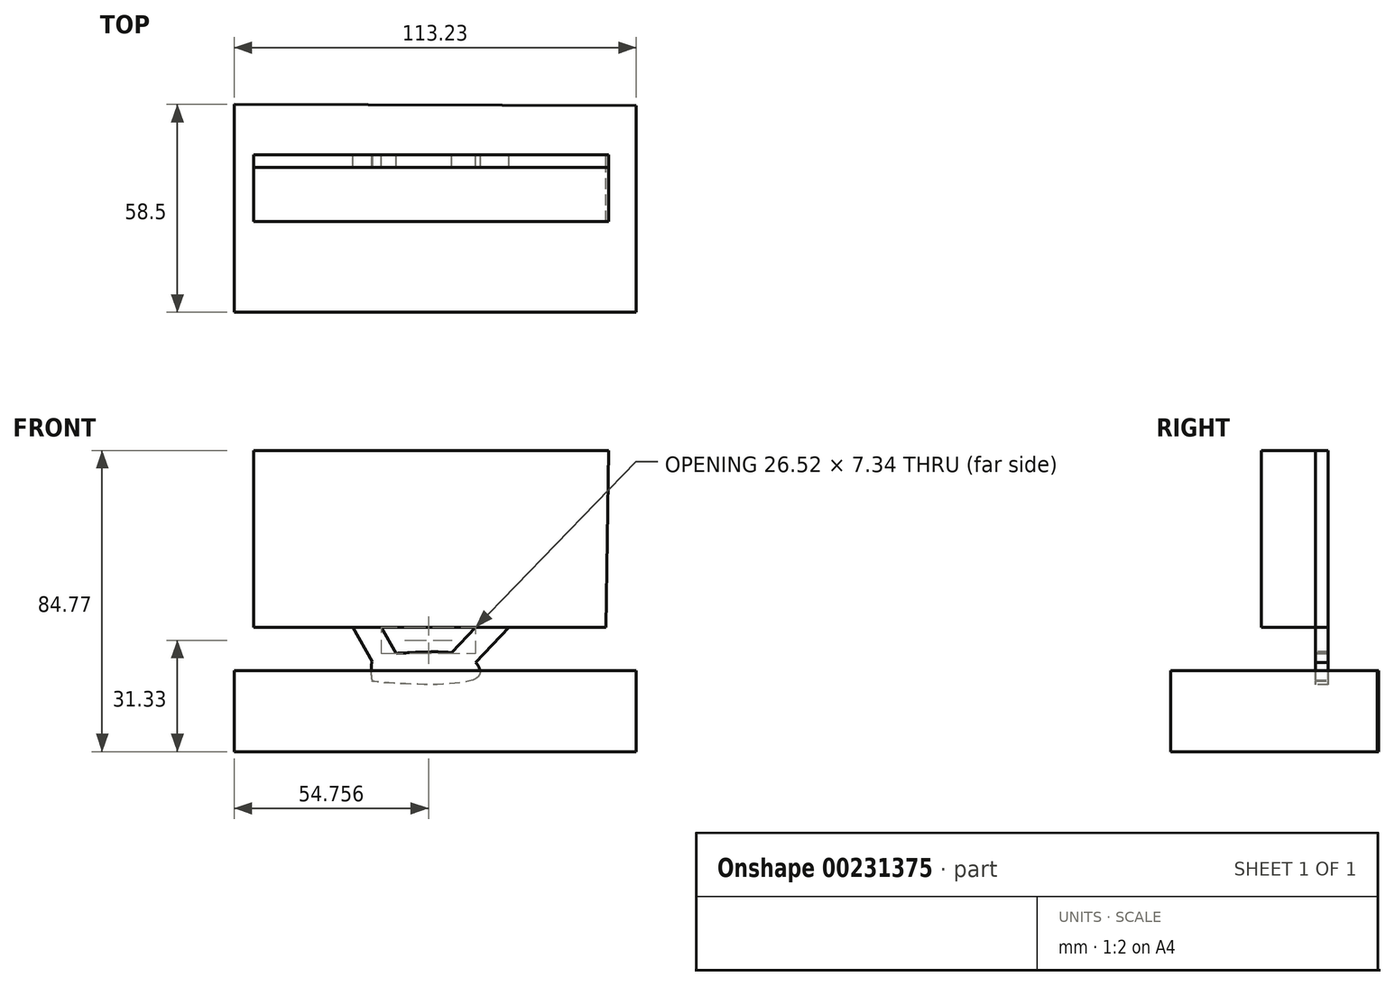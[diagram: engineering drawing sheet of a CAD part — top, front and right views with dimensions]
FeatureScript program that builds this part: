
annotation { "Feature Type Name" : "Feature", "Feature Type Description" : "" }
export const myFeature = defineFeature(function(context is Context, id is Id, definition is map)
    precondition{}
    {
        {
            var Q0;
            Q0=qCreatedBy(makeId("Top.planeOp"),FACE);
            var sketch = newSketch(context, id + "F0", { "sketchPlane" : qUnion([Q0])});
            skLineSegment(sketch, "E0", {"start": v(-55.92, 14.18) * mm, "end": v(-55.92, -44.32) * mm});
            skLineSegment(sketch, "E1", {"start": v(-55.92, -44.32) * mm, "end": v(57.3, -44.32) * mm});
            skLineSegment(sketch, "E2", {"start": v(57.3, -44.32) * mm, "end": v(57.3, 13.78) * mm});
            skLineSegment(sketch, "E3", {"start": v(57.3, 13.78) * mm, "end": v(-55.92, 14.18) * mm});
            skSolve(sketch);
        }
        {
            var Q0;
            Q0 = qSketchRegion(id + "F0", true);
            extrude(context, id + "F1", {"entities" : qUnion([Q0]), "depth" : 22.86 * mm});
        }
        {
            var Q0;
            Q0=qCreatedBy(makeId("Front.planeOp"),FACE);
            var sketch = newSketch(context, id + "F2", { "sketchPlane" : qUnion([Q0])});
            skLineSegment(sketch, "E4", {"start": v(-17.05, 25.28) * mm, "end": v(-22.5, 35) * mm});
            skLineSegment(sketch, "E5", {"start": v(-10.31, 27.66) * mm, "end": v(-14.42, 35) * mm});
            skLineSegment(sketch, "E6", {"start": v(5.35, 27.86) * mm, "end": v(12.1, 35) * mm});
            skLineSegment(sketch, "E7", {"start": v(12.1, 25.08) * mm, "end": v(21.46, 35) * mm});
            skLineSegment(sketch, "E8", {"start": v(-14.42, 35) * mm, "end": v(-50.37, 35) * mm});
            skLineSegment(sketch, "E9", {"start": v(-50.37, 35) * mm, "end": v(-50.37, 84.77) * mm});
            skLineSegment(sketch, "E10", {"start": v(-50.37, 84.77) * mm, "end": v(49.57, 84.77) * mm});
            skLineSegment(sketch, "E11", {"start": v(-14.42, 35) * mm, "end": v(48.78, 35) * mm});
            skLineSegment(sketch, "E12", {"start": v(49.57, 84.77) * mm, "end": v(48.78, 35) * mm});
            skFitSpline(sketch, "E13", {"points": [v(-17.05, 25.28) * mm, v(-10.31, 27.66) * mm, v(5.35, 27.86) * mm, v(12.1, 25.08) * mm, v(12.1, 20.55) * mm, v(-17.05, 19.8) * mm, v(-17.05, 19.87) * mm, v(-17.05, 25.28) * mm]});
            skLineSegment(sketch, "E14", {"start": v(-17.05, 19.87) * mm, "end": v(12.1, 20.55) * mm});
            skLineSegment(sketch, "E15", {"start": v(12.1, 20.55) * mm, "end": v(12.1, 25.08) * mm});
            skLineSegment(sketch, "E16", {"start": v(-17.05, 25.28) * mm, "end": v(-17.05, 19.87) * mm});
            skSolve(sketch);
        }
        {
            var Q0;
            {var subQ0=sQuery(id+"F2.wireOp",EDGE,"E9");Q0=makeQuery(id+"F2.imprint","IMPRINT",FACE,{"disambiguationData":[TD([[makeQuery(id+"F2.imprint","IMPRINT",EDGE,{"derivedFrom":subQ0}),-1.0]])]});}
            extrude(context, id + "F3", {"entities" : qUnion([Q0]), "depth" : 18.8 * mm});
        }
        {
            var Q0;
            Q0 = qSketchRegion(id + "F2", true);
            extrude(context, id + "F4", {"entities" : qUnion([Q0]), "depth" : 3.56 * mm});
        }
    });
